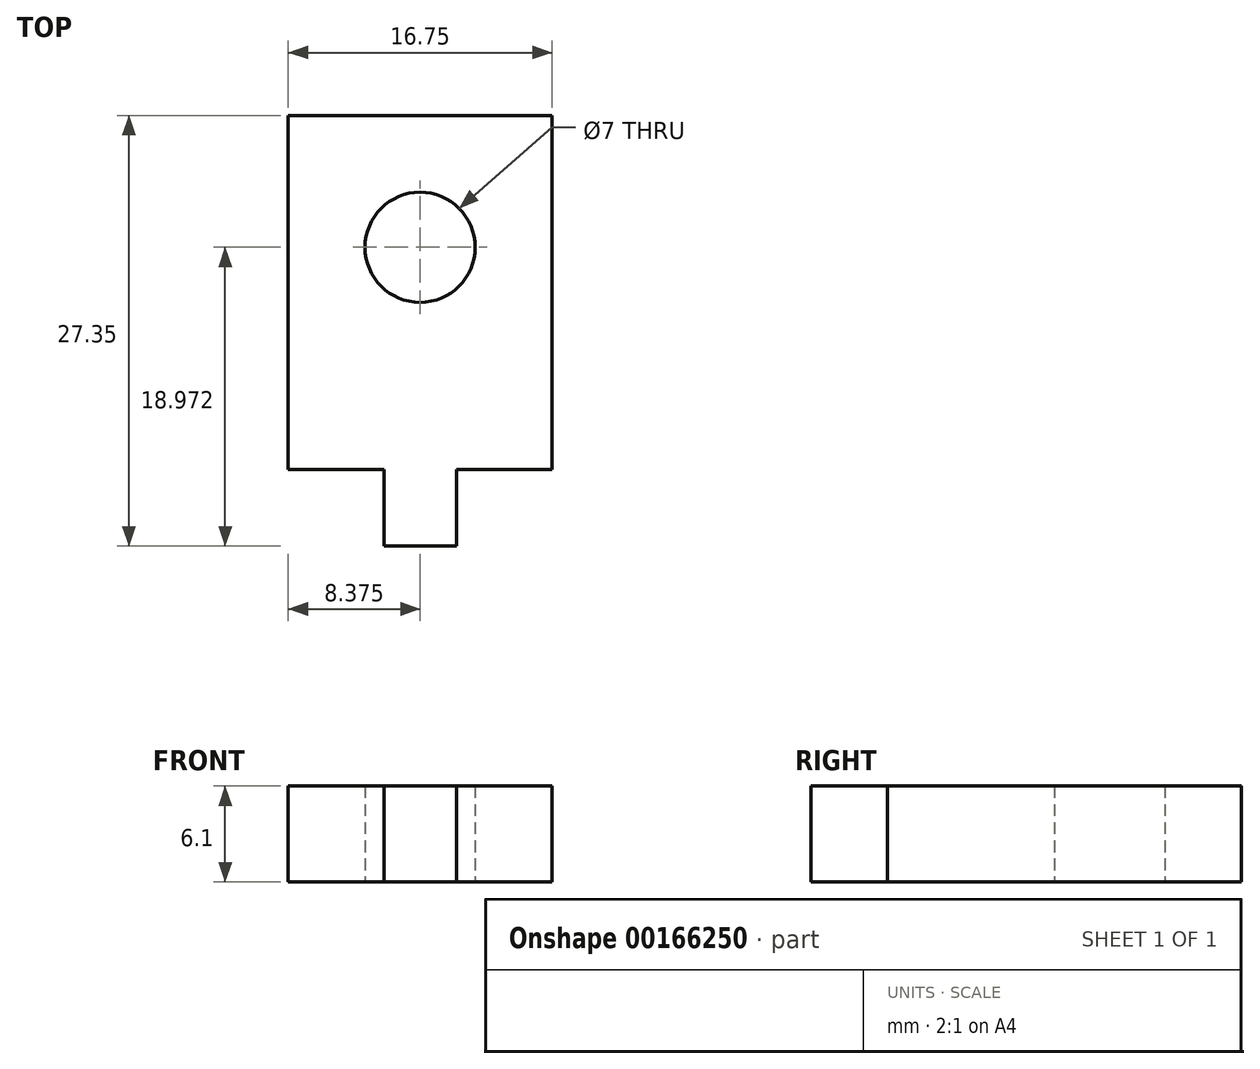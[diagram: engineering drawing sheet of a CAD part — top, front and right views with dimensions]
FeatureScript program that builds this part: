
annotation { "Feature Type Name" : "Feature", "Feature Type Description" : "" }
export const myFeature = defineFeature(function(context is Context, id is Id, definition is map)
    precondition{}
    {
        {
            var Q0;
            Q0=qCreatedBy(makeId("Top.planeOp"),FACE);
            var sketch = newSketch(context, id + "F0", { "sketchPlane" : qUnion([Q0])});
            skLineSegment(sketch, "E0.bottom", {"start": v(5.01, 11.48) * mm, "end": v(21.76, 11.48) * mm});
            skLineSegment(sketch, "E0.top", {"start": v(5.01, -11.02) * mm, "end": v(11.09, -11.02) * mm});
            skLineSegment(sketch, "E0.left", {"start": v(5.01, 11.48) * mm, "end": v(5.01, -11.02) * mm});
            skLineSegment(sketch, "E0.right", {"start": v(21.76, 11.48) * mm, "end": v(21.76, -11.02) * mm});
            skLineSegment(sketch, "E1.bottom", {"start": v(15.69, -15.87) * mm, "end": v(11.09, -15.87) * mm});
            skLineSegment(sketch, "E1.left", {"start": v(15.69, -15.87) * mm, "end": v(15.69, -11.02) * mm});
            skLineSegment(sketch, "E1.right", {"start": v(11.09, -15.87) * mm, "end": v(11.09, -11.02) * mm});
            skLineSegment(sketch, "E2.trimOffspring", {"start": v(15.69, -11.02) * mm, "end": v(21.76, -11.02) * mm});
            skCircle(sketch, "E3", {"center": v(13.39, 3.1) * mm, "radius": 3.5 * mm});
            skSolve(sketch);
        }
        {
            var Q0;
            Q0 = qSketchRegion(id + "F0", true);
            extrude(context, id + "F1", {"entities" : qUnion([Q0]), "depth" : 6.1 * mm});
        }
    });
